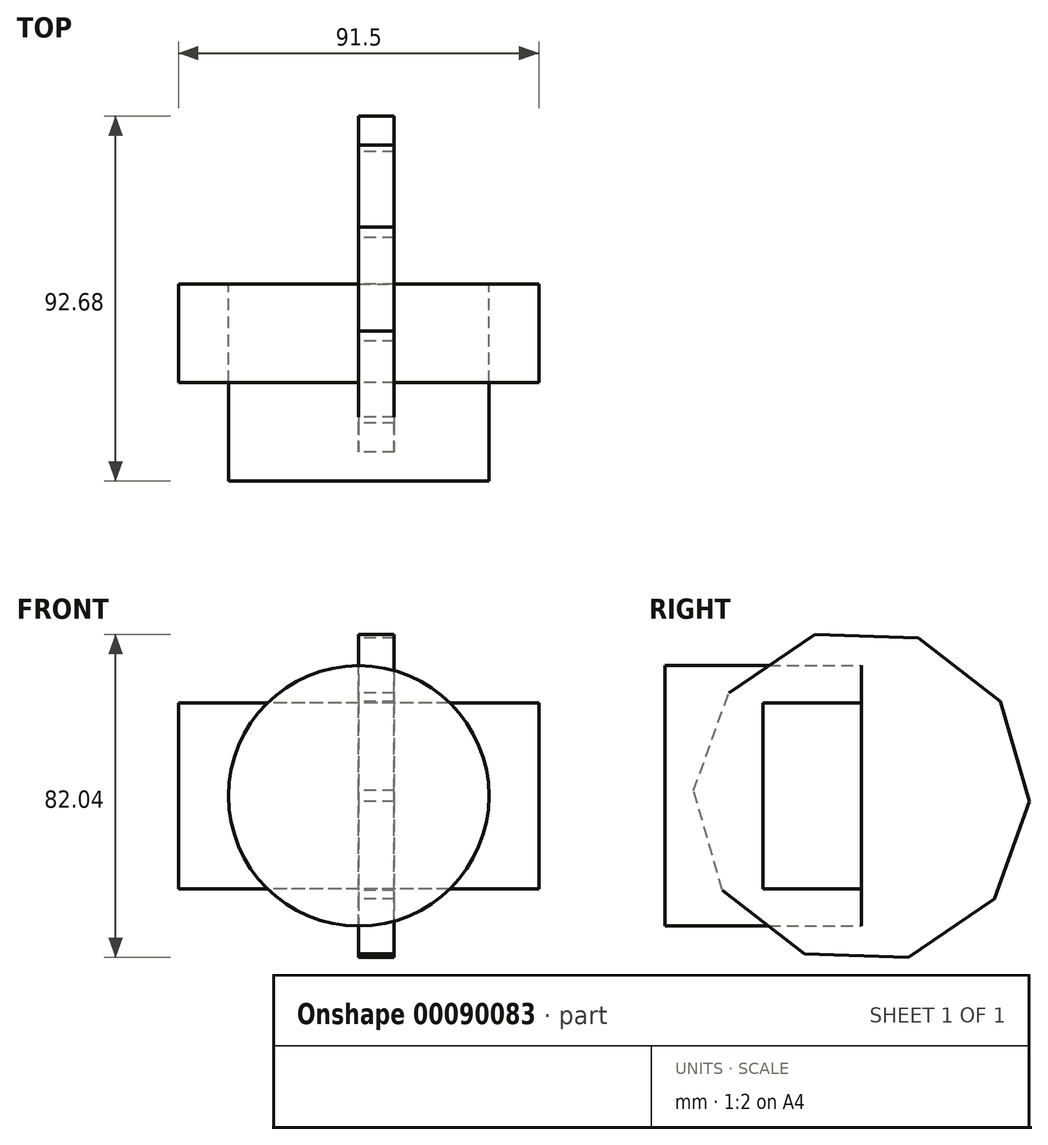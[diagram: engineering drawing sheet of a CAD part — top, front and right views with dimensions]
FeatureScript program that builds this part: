
annotation { "Feature Type Name" : "Feature", "Feature Type Description" : "" }
export const myFeature = defineFeature(function(context is Context, id is Id, definition is map)
    precondition{}
    {
        {
            var Q0;
            Q0=qCreatedBy(makeId("Front.planeOp"),FACE);
            var sketch = newSketch(context, id + "F0", { "sketchPlane" : qUnion([Q0])});
            skLineSegment(sketch, "E0.bottom", {"start": v(45.75, -23.61) * mm, "end": v(-45.75, -23.61) * mm});
            skLineSegment(sketch, "E0.top", {"start": v(45.75, 23.61) * mm, "end": v(-45.75, 23.61) * mm});
            skLineSegment(sketch, "E0.left", {"start": v(45.75, -23.61) * mm, "end": v(45.75, 23.61) * mm});
            skLineSegment(sketch, "E0.right", {"start": v(-45.75, -23.61) * mm, "end": v(-45.75, 23.61) * mm});
            skPoint(sketch, "E0.middle", {"position": v(0, 0) * mm});
            skSolve(sketch);
        }
        {
            var Q0;
            Q0 = qSketchRegion(id + "F0", true);
            extrude(context, id + "F1", {"entities" : qUnion([Q0]), "depth" : 25 * mm});
        }
        {
            var Q0;
            Q0=qCreatedBy(makeId("Front.planeOp"),FACE);
            var sketch = newSketch(context, id + "F2", { "sketchPlane" : qUnion([Q0])});
            skCircle(sketch, "E1", {"center": v(0, 0) * mm, "radius": 33.09 * mm});
            skSolve(sketch);
        }
        {
            var Q0;
            Q0=makeQuery(id+"F2.imprint","IMPRINT",FACE,{"disambiguationData":[TD([[makeQuery(id+"F2.imprint","IMPRINT",EDGE,{"derivedFrom":sQuery(id+"F2.wireOp",EDGE,"E1")}),1.0]])]});
            extrude(context, id + "F3", {"entities" : qUnion([Q0]), "depth" : 50 * mm});
        }
        {
            var Q0;
            Q0=qCreatedBy(makeId("Right.planeOp"),FACE);
            var sketch = newSketch(context, id + "F4", { "sketchPlane" : qUnion([Q0])});
            skCircle(sketch, "E2.cCircle", {"center": v(0, 0) * mm, "radius": 40.6 * mm, "construction": true});
            skLineSegment(sketch, "E2.0", {"start": v(35.34, 23.97) * mm, "end": v(42.68, -1.38) * mm});
            skLineSegment(sketch, "E2.1", {"start": v(42.68, -1.38) * mm, "end": v(33.71, -26.2) * mm});
            skLineSegment(sketch, "E2.2", {"start": v(33.71, -26.2) * mm, "end": v(11.87, -41.02) * mm});
            skLineSegment(sketch, "E2.3", {"start": v(11.87, -41.02) * mm, "end": v(-14.5, -40.16) * mm});
            skLineSegment(sketch, "E2.4", {"start": v(-14.5, -40.16) * mm, "end": v(-35.34, -23.97) * mm});
            skLineSegment(sketch, "E2.5", {"start": v(-35.34, -23.97) * mm, "end": v(-42.68, 1.38) * mm});
            skLineSegment(sketch, "E2.6", {"start": v(-42.68, 1.38) * mm, "end": v(-33.71, 26.2) * mm});
            skLineSegment(sketch, "E2.7", {"start": v(-33.71, 26.2) * mm, "end": v(-11.87, 41.02) * mm});
            skLineSegment(sketch, "E2.8", {"start": v(-11.87, 41.02) * mm, "end": v(14.5, 40.16) * mm});
            skLineSegment(sketch, "E2.9", {"start": v(14.5, 40.16) * mm, "end": v(35.34, 23.97) * mm});
            skPoint(sketch, "E2.0.midPoint", {"position": v(39, 11.3) * mm});
            skSolve(sketch);
        }
        {
            var Q0;
            Q0=makeQuery(id+"F4.imprint","IMPRINT",FACE,{"disambiguationData":[TD([[makeQuery(id+"F4.imprint","IMPRINT",EDGE,{"derivedFrom":sQuery(id+"F4.wireOp",EDGE,"E2.0")}),-1.0]])]});
            extrude(context, id + "F5", {"entities" : qUnion([Q0]), "depth" : 9 * mm});
        }
    });
